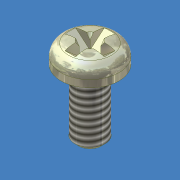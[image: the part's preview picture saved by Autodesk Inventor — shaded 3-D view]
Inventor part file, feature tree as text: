
AUTODESK INVENTOR PART (.ipt)
format: ipt  version: 2012 (Build 160160000, 160)  size: 184,832 bytes
history: native  units: mm (DEFAULTED — no unit token found)
features: other x29, sketch x4, extrude x3, revolve x1, thread x1, chamfer x1
ambient origin geometry x8: Origin, YZ Plane, XZ Plane, XY Plane, X Axis, Y Axis, Z Axis, Center Point
bodies: Solid1 (feature_tree)
feature tree (39):
  other  "Table"
  other  "Size = 2-56 UNC"
  other  "Length = 0.188"
  other  "Length = 0.375"
  other  "Length = 0.438"
  other  "Length = 0.625"
  other  "Length = 0.875"
  other  "Size = 4-40 UNC"
  other  "Length = 0.125"
  other  "Length = 0.313"
  other  "Size = 5-40 UNC"
  other  "Size = 6-32 UNC"
  other  "Size = 8-32 UNC"
  other  "Size = 10-24 UNC"
  other  "Size = 10-32 UNF"
  other  "Size = 1/4-20 UNC"
  other  "Size = 5/16-18 UNC"
  other  "Size = 3/8-16 UNC"
  other  "Length = 0.25"
  other  "Length = 0.75"
  other  "Length = 1"
  other  "Length = 0.5"
  other  "Length = 1.25"
  other  "Length = 1.5"
  other  "Length = 1.75"
  other  "Length = 2"
  other  "Length = 4"
  other  "Length = 2.5"
  other  "Length = 3"
  revolve  "Revolution1"  [1 undecoded]
  extrude  "Extrusion1"  Depth=2.1209mm
  extrude  "Extrusion2"  Depth=1.52908mm
  extrude  "Extrusion3"  Depth=1.3462mm
  thread  "Thread1"  [1 undecoded]
  chamfer  "Chamfer1"  Distance=0.7874mm
  sketch  "Sketch1"  dims[d0=2.1844mm d1=4.2418mm]
  sketch  "Sketch2"  dims[d2=0.889mm d3=2.1209mm]
  sketch  "Sketch3"  dims[d4=4.7752mm d6=1.52908mm]
  sketch  "Sketch4"  dims[d7=90.0deg d8=1.3462mm d9=3.18135mm d10=0.7874mm d11=0.0mm d12=3.18135mm d13=0.7874mm d14=0.0mm d15=0.76454mm d16=-5.235988mm d17=1.52908mm d18=4.5466mm d19=0.0mm d20=0.27305mm d21=0.27305mm d22=1.3462mm d23=45.0deg]
note: 2 required parameter values undecoded (feature->parameter linkage not recoverable at this tier; creation-order binding heuristic only, values carry confidence <= 0.55)